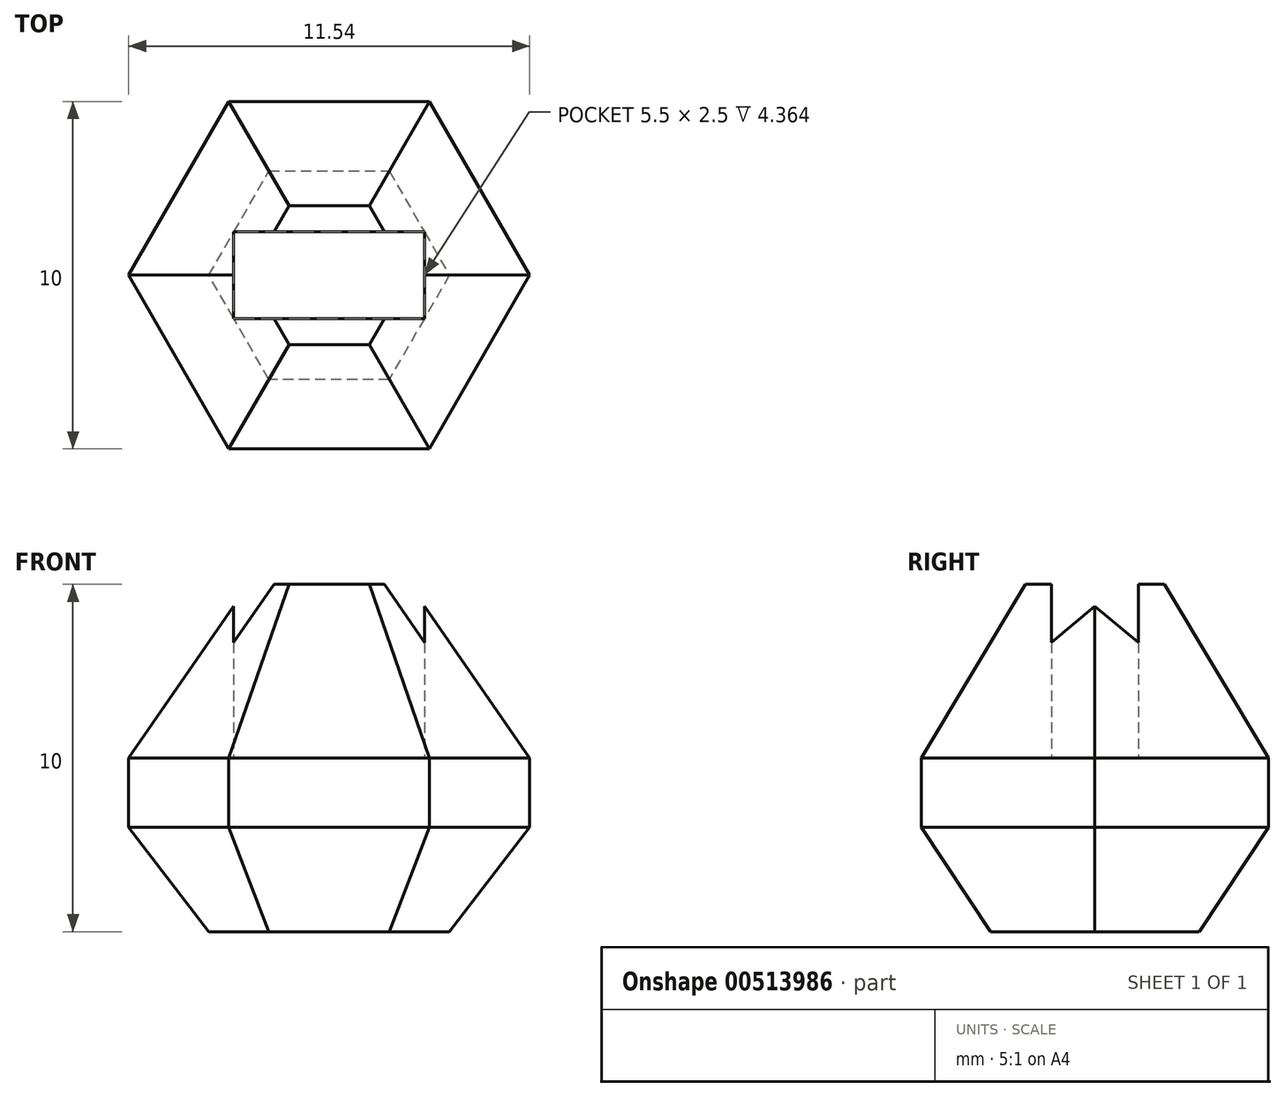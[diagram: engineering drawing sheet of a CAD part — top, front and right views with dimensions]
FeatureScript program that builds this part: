
annotation { "Feature Type Name" : "Feature", "Feature Type Description" : "" }
export const myFeature = defineFeature(function(context is Context, id is Id, definition is map)
    precondition{}
    {
        {
            var Q0;
            Q0=qCreatedBy(makeId("Top.planeOp"),FACE);
            var sketch = newSketch(context, id + "F0", { "sketchPlane" : qUnion([Q0])});
            skCircle(sketch, "E0.cCircle", {"center": v(0, 0) * mm, "radius": 5 * mm, "construction": true});
            skLineSegment(sketch, "E0.0", {"start": v(-2.89, 5) * mm, "end": v(2.89, 5) * mm});
            skLineSegment(sketch, "E0.1", {"start": v(2.89, 5) * mm, "end": v(5.77, 0) * mm});
            skLineSegment(sketch, "E0.2", {"start": v(5.77, 0) * mm, "end": v(2.89, -5) * mm});
            skLineSegment(sketch, "E0.3", {"start": v(2.89, -5) * mm, "end": v(-2.89, -5) * mm});
            skLineSegment(sketch, "E0.4", {"start": v(-2.89, -5) * mm, "end": v(-5.77, 0) * mm});
            skLineSegment(sketch, "E0.5", {"start": v(-5.77, 0) * mm, "end": v(-2.89, 5) * mm});
            skPoint(sketch, "E0.0.midPoint", {"position": v(0, 5) * mm});
            skLineSegment(sketch, "E1.bottom", {"start": v(-2.75, 1.25) * mm, "end": v(2.75, 1.25) * mm});
            skLineSegment(sketch, "E1.top", {"start": v(-2.75, -1.25) * mm, "end": v(2.75, -1.25) * mm});
            skLineSegment(sketch, "E1.left", {"start": v(-2.75, 1.25) * mm, "end": v(-2.75, -1.25) * mm});
            skLineSegment(sketch, "E1.right", {"start": v(2.75, 1.25) * mm, "end": v(2.75, -1.25) * mm});
            skSolve(sketch);
        }
        {
            var Q0;
            Q0=makeQuery(id+"F0.imprint","IMPRINT",FACE,{"disambiguationData":[TD([[makeQuery(id+"F0.imprint","IMPRINT",EDGE,{"derivedFrom":sQuery(id+"F0.wireOp",EDGE,"E0.0")}),-1.0]])]});
            extrude(context, id + "F1", {"entities" : qUnion([Q0]), "depth" : 10 * mm});
        }
        {
            var Q0;
            Q0=makeQuery(id+"F1.opExtrude","CAP_EDGE",EDGE,{"disambiguationData":[OSD([sQuery(id+"F0.wireOp",EDGE,"E0.0")])],"isStart":true});
            var Q1;
            Q1=makeQuery(id+"F1.opExtrude","CAP_EDGE",EDGE,{"disambiguationData":[OSD([sQuery(id+"F0.wireOp",EDGE,"E0.1")])],"isStart":true});
            var Q2;
            Q2=makeQuery(id+"F1.opExtrude","CAP_EDGE",EDGE,{"disambiguationData":[OSD([sQuery(id+"F0.wireOp",EDGE,"E0.5")])],"isStart":true});
            var Q3;
            Q3=makeQuery(id+"F1.opExtrude","CAP_EDGE",EDGE,{"disambiguationData":[OSD([sQuery(id+"F0.wireOp",EDGE,"E0.4")])],"isStart":true});
            var Q4;
            Q4=makeQuery(id+"F1.opExtrude","CAP_EDGE",EDGE,{"disambiguationData":[OSD([sQuery(id+"F0.wireOp",EDGE,"E0.3")])],"isStart":true});
            var Q5;
            Q5=makeQuery(id+"F1.opExtrude","CAP_EDGE",EDGE,{"disambiguationData":[OSD([sQuery(id+"F0.wireOp",EDGE,"E0.2")])],"isStart":true});
            chamfer(context, id + "F2", {"entities" : qUnion([Q0, Q1, Q2, Q3, Q4, Q5]), "chamferType" : ChamferType.TWO_OFFSETS, "width1" : 2 * mm, "oppositeDirection" : false, "width2" : 3 * mm, "tangentPropagation" : true});
        }
        {
            var Q0;
            Q0=makeQuery(id+"F1.opExtrude","CAP_EDGE",EDGE,{"disambiguationData":[OSD([sQuery(id+"F0.wireOp",EDGE,"E0.1")])],"isStart":false});
            var Q1;
            Q1=makeQuery(id+"F1.opExtrude","CAP_EDGE",EDGE,{"disambiguationData":[OSD([sQuery(id+"F0.wireOp",EDGE,"E0.0")])],"isStart":false});
            var Q2;
            Q2=makeQuery(id+"F1.opExtrude","CAP_EDGE",EDGE,{"disambiguationData":[OSD([sQuery(id+"F0.wireOp",EDGE,"E0.5")])],"isStart":false});
            var Q3;
            Q3=makeQuery(id+"F1.opExtrude","CAP_EDGE",EDGE,{"disambiguationData":[OSD([sQuery(id+"F0.wireOp",EDGE,"E0.4")])],"isStart":false});
            var Q4;
            Q4=makeQuery(id+"F1.opExtrude","CAP_EDGE",EDGE,{"disambiguationData":[OSD([sQuery(id+"F0.wireOp",EDGE,"E0.3")])],"isStart":false});
            var Q5;
            Q5=makeQuery(id+"F1.opExtrude","CAP_EDGE",EDGE,{"disambiguationData":[OSD([sQuery(id+"F0.wireOp",EDGE,"E0.2")])],"isStart":false});
            chamfer(context, id + "F3", {"entities" : qUnion([Q0, Q1, Q2, Q3, Q4, Q5]), "chamferType" : ChamferType.TWO_OFFSETS, "width1" : 5 * mm, "oppositeDirection" : false, "width2" : 3 * mm, "tangentPropagation" : true});
        }
        {
            var Q0;
            Q0=makeQuery(id+"F0.imprint","IMPRINT",FACE,{"disambiguationData":[TD([[makeQuery(id+"F0.imprint","IMPRINT",EDGE,{"derivedFrom":sQuery(id+"F0.wireOp",EDGE,"E1.bottom")}),-1.0]])]});
            extrude(context, id + "F4", {"entities" : qUnion([Q0]), "operationType" : NewBodyOperationType.ADD, "depth" : 5 * mm});
        }
    });
